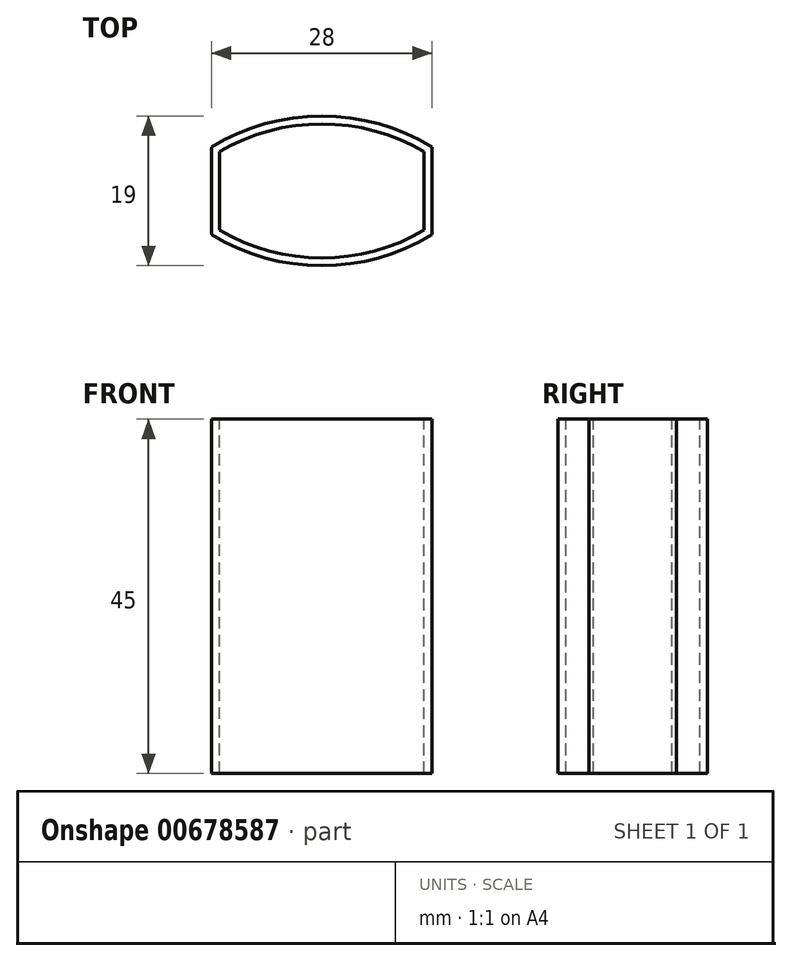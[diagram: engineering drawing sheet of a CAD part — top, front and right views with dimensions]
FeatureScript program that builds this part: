
annotation { "Feature Type Name" : "Feature", "Feature Type Description" : "" }
export const myFeature = defineFeature(function(context is Context, id is Id, definition is map)
    precondition{}
    {
        {
            var Q0;
            Q0=qCreatedBy(makeId("Top.planeOp"),FACE);
            var sketch = newSketch(context, id + "F0", { "sketchPlane" : qUnion([Q0])});
            skLineSegment(sketch, "E0", {"start": v(-40.38, -5.94) * mm, "end": v(-40.38, -15.94) * mm});
            skLineSegment(sketch, "E1", {"start": v(-14.38, -5.94) * mm, "end": v(-14.38, -15.94) * mm});
            skArc(sketch, "E2", {"start": v(-14.38, -5.94) * mm, "mid": v(-27.38, -2.44) * mm, "end": v(-40.38, -5.94) * mm});
            skArc(sketch, "E3", {"start": v(-40.38, -15.94) * mm, "mid": v(-27.38, -19.44) * mm, "end": v(-14.38, -15.94) * mm});
            skArc(sketch, "E4.0", {"start": v(-13.38, -5.37) * mm, "mid": v(-27.38, -1.44) * mm, "end": v(-41.38, -5.37) * mm});
            skLineSegment(sketch, "E4.1", {"start": v(-13.38, -5.37) * mm, "end": v(-13.38, -16.5) * mm});
            skArc(sketch, "E4.2", {"start": v(-41.38, -16.5) * mm, "mid": v(-27.38, -20.44) * mm, "end": v(-13.38, -16.5) * mm});
            skLineSegment(sketch, "E4.3", {"start": v(-41.38, -5.37) * mm, "end": v(-41.38, -16.5) * mm});
            skSolve(sketch);
        }
        {
            var Q0;
            Q0=sQuery(id+"F0.wireOp",EDGE,"E4.0");
            var Q1;
            Q1=sQuery(id+"F0.wireOp",EDGE,"E2");
            var Q2;
            Q2=sQuery(id+"F0.wireOp",EDGE,"E0");
            var Q3;
            Q3=sQuery(id+"F0.wireOp",EDGE,"E4.3");
            var Q4;
            Q4=sQuery(id+"F0.wireOp",EDGE,"E3");
            var Q5;
            Q5=sQuery(id+"F0.wireOp",EDGE,"E4.2");
            var Q6;
            Q6=sQuery(id+"F0.wireOp",EDGE,"E1");
            var Q7;
            Q7=sQuery(id+"F0.wireOp",EDGE,"E4.1");
            extrude(context, id + "F1", {"bodyType" : ToolBodyType.SURFACE, "surfaceEntities" : qUnion([Q0, Q1, Q2, Q3, Q4, Q5, Q6, Q7]), "depth" : 45 * mm, "offsetDistance" : 25 * mm});
        }
    });
